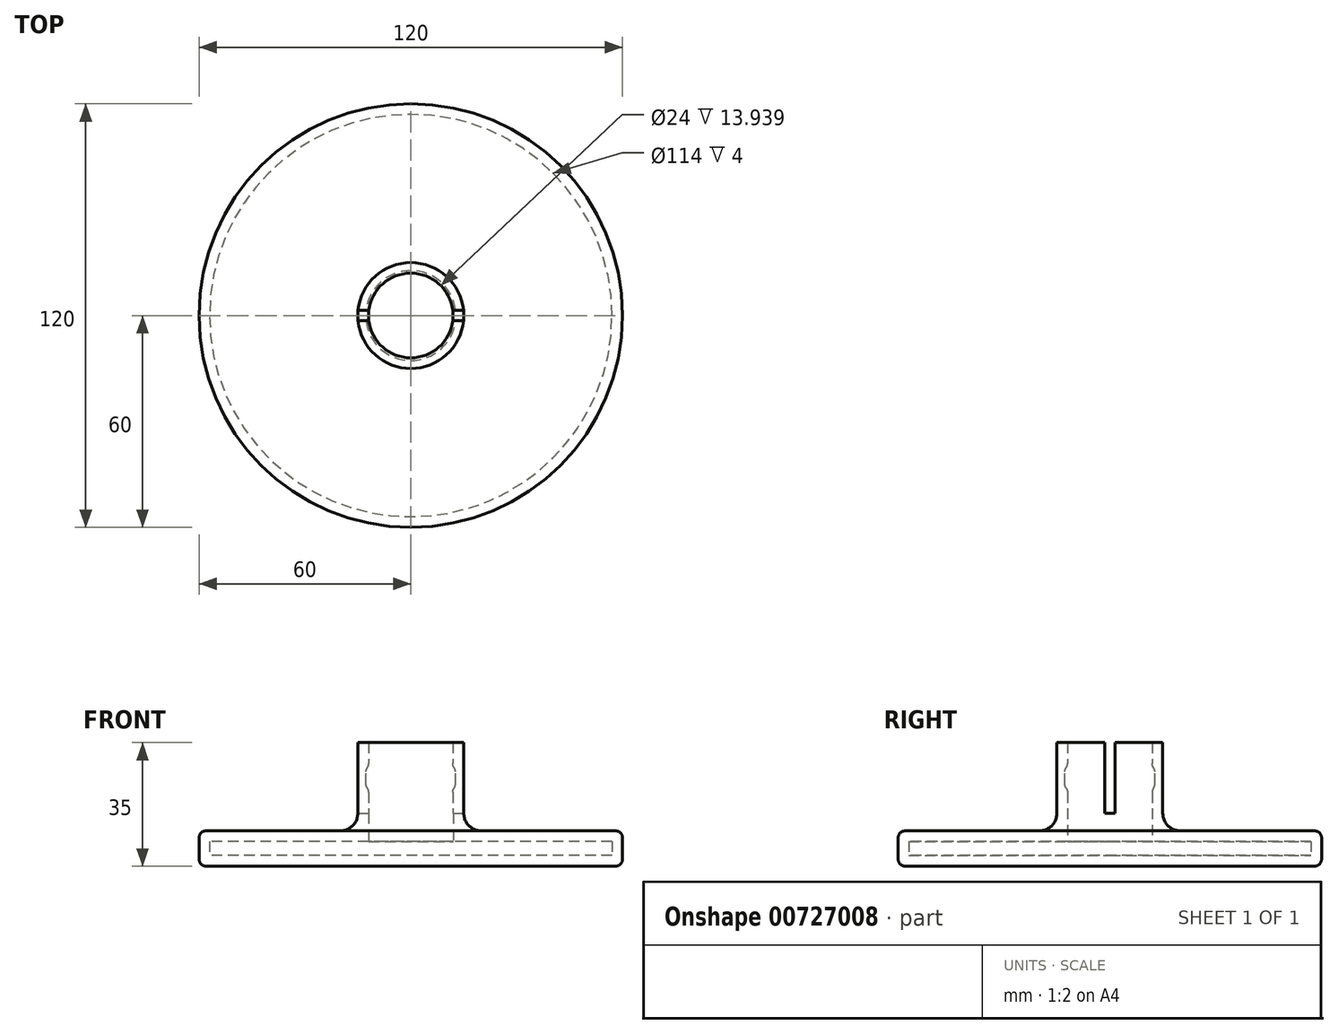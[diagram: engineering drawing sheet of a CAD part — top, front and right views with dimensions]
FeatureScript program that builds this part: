
annotation { "Feature Type Name" : "Feature", "Feature Type Description" : "" }
export const myFeature = defineFeature(function(context is Context, id is Id, definition is map)
    precondition{}
    {
        {
            var Q0;
            Q0=qCreatedBy(makeId("Top.planeOp"),FACE);
            var sketch = newSketch(context, id + "F0", { "sketchPlane" : qUnion([Q0])});
            skCircle(sketch, "E0", {"center": v(0, 0) * mm, "radius": 60 * mm});
            skCircle(sketch, "E1", {"center": v(0, 0) * mm, "radius": 15 * mm});
            skSolve(sketch);
        }
        {
            var Q0;
            Q0 = qSketchRegion(id + "F0", true);
            var Q1;
            Q1=makeQuery(id+"F0.imprint","IMPRINT",FACE,{"disambiguationData":[TD([[makeQuery(id+"F0.imprint","IMPRINT",EDGE,{"derivedFrom":sQuery(id+"F0.wireOp",EDGE,"E1")}),1.0]])]});
            extrude(context, id + "F1", {"entities" : qUnion([Q0, Q1]), "depth" : 10 * mm, "offsetDistance" : 25 * mm});
        }
        {
            var Q0;
            Q0=makeQuery(id+"F0.imprint","IMPRINT",FACE,{"disambiguationData":[TD([[makeQuery(id+"F0.imprint","IMPRINT",EDGE,{"derivedFrom":sQuery(id+"F0.wireOp",EDGE,"E1")}),1.0]])]});
            extrude(context, id + "F2", {"entities" : qUnion([Q0]), "operationType" : NewBodyOperationType.ADD, "depth" : 35 * mm, "offsetDistance" : 25 * mm});
        }
        {
            var Q0;
            Q0=makeQuery(id+"F2.opExtrude","CAP_FACE",FACE,{"disambiguationData":[OSD([sQuery(id+"F0.wireOp",EDGE,"E1")])],"isStart":false});
            shell(context, id + "F3", {"entities" : qUnion([Q0]), "thickness" : 3 * mm});
        }
        {
            var Q0;
            Q0=qCreatedBy(makeId("Right.planeOp"),FACE);
            var sketch = newSketch(context, id + "F4", { "sketchPlane" : qUnion([Q0])});
            skLineSegment(sketch, "E2.bottom", {"start": v(-1.5, 15) * mm, "end": v(1.5, 15) * mm});
            skLineSegment(sketch, "E2.top", {"start": v(-1.5, 35) * mm, "end": v(1.5, 35) * mm});
            skLineSegment(sketch, "E2.left", {"start": v(-1.5, 15) * mm, "end": v(-1.5, 35) * mm});
            skLineSegment(sketch, "E2.right", {"start": v(1.5, 15) * mm, "end": v(1.5, 35) * mm});
            skSolve(sketch);
        }
        {
            var Q0;
            Q0=makeQuery(id+"F4.imprint","IMPRINT",FACE,{"disambiguationData":[TD([[makeQuery(id+"F4.imprint","IMPRINT",EDGE,{"derivedFrom":sQuery(id+"F4.wireOp",EDGE,"E2.bottom")}),1.0]])]});
            extrude(context, id + "F5", {"entities" : qUnion([Q0]), "operationType" : NewBodyOperationType.REMOVE, "endBound" : BoundingType.SYMMETRIC, "oppositeDirection" : true, "depth" : 50 * mm, "offsetDistance" : 25 * mm});
        }
        {
            var Q0;
            Q0=qCreatedBy(makeId("Top.planeOp"),FACE);
            cPlane(context, id + "F6", {"entities" : qUnion([Q0]), "cplaneType" : CPlaneType.OFFSET, "offset" : 25 * mm, "width" : 150 * mm, "height" : 150 * mm});
        }
        {
            var Q0;
            Q0=qCreatedBy(id+"F6.planeOp",FACE);
            var sketch = newSketch(context, id + "F7", { "sketchPlane" : qUnion([Q0])});
            skCircle(sketch, "E3", {"center": v(0, 0) * mm, "radius": 12.75 * mm});
            skSolve(sketch);
        }
        {
            var Q0;
            Q0=makeQuery(id+"F7.imprint","IMPRINT",FACE,{"disambiguationData":[TD([[makeQuery(id+"F7.imprint","IMPRINT",EDGE,{"derivedFrom":sQuery(id+"F7.wireOp",EDGE,"E3")}),1.0]])]});
            extrude(context, id + "F8", {"entities" : qUnion([Q0]), "operationType" : NewBodyOperationType.REMOVE, "endBound" : BoundingType.SYMMETRIC, "oppositeDirection" : true, "depth" : 5 * mm, "offsetDistance" : 25 * mm});
        }
        {
            var Q0;
            Q0=makeQuery(id+"F2.boolean.opBoolean","INTERSECT",EDGE,{"derivedFrom":[makeQuery(id+"F1.opExtrude","CAP_FACE",FACE,{"disambiguationData":[OSD([sQuery(id+"F0.wireOp",EDGE,"E0")])],"isStart":false}),makeQuery(id+"F2.opExtrude","SWEPT_FACE",FACE,{"disambiguationData":[OSD([sQuery(id+"F0.wireOp",EDGE,"E1")])]})]});
            fillet(context, id + "F9", {"entities" : qUnion([Q0]), "radius" : 5 * mm, "tangentPropagation" : true, "allowEdgeOverflow" : false});
        }
        {
            var Q0;
            Q0=makeQuery(id+"F1.opExtrude","CAP_EDGE",EDGE,{"disambiguationData":[OSD([sQuery(id+"F0.wireOp",EDGE,"E0")])],"isStart":false});
            var Q1;
            Q1=makeQuery(id+"F1.opExtrude","CAP_EDGE",EDGE,{"disambiguationData":[OSD([sQuery(id+"F0.wireOp",EDGE,"E0")])],"isStart":true});
            fillet(context, id + "F10", {"entities" : qUnion([Q0, Q1]), "radius" : 2 * mm, "tangentPropagation" : true, "allowEdgeOverflow" : false});
        }
        {
            var Q0;
            Q0=makeQuery(id+"F8.boolean.opBoolean","INTERSECT",EDGE,{"disambiguationData":[OD(1.0)],"derivedFrom":[makeQuery(id+"F3.opShell","OFFSET_FACE",FACE,{"disambiguationData":[OSD([sQuery(id+"F0.wireOp",EDGE,"E1")])]}),makeQuery(id+"F8.opExtrude","CAP_FACE",FACE,{"disambiguationData":[OSD([sQuery(id+"F7.wireOp",EDGE,"E3")])],"isStart":false})]});
            var Q1;
            Q1=makeQuery(id+"F8.boolean.opBoolean","INTERSECT",EDGE,{"disambiguationData":[OD(1.0)],"derivedFrom":[makeQuery(id+"F3.opShell","OFFSET_FACE",FACE,{"disambiguationData":[OSD([sQuery(id+"F0.wireOp",EDGE,"E1")])]}),makeQuery(id+"F8.opExtrude","CAP_FACE",FACE,{"disambiguationData":[OSD([sQuery(id+"F7.wireOp",EDGE,"E3")])],"isStart":true})]});
            var Q2;
            Q2=makeQuery(id+"F8.boolean.opBoolean","INTERSECT",EDGE,{"disambiguationData":[OD(0.0)],"derivedFrom":[makeQuery(id+"F3.opShell","OFFSET_FACE",FACE,{"disambiguationData":[OSD([sQuery(id+"F0.wireOp",EDGE,"E1")])]}),makeQuery(id+"F8.opExtrude","CAP_FACE",FACE,{"disambiguationData":[OSD([sQuery(id+"F7.wireOp",EDGE,"E3")])],"isStart":false})]});
            var Q3;
            Q3=makeQuery(id+"F8.boolean.opBoolean","INTERSECT",EDGE,{"disambiguationData":[OD(0.0)],"derivedFrom":[makeQuery(id+"F3.opShell","OFFSET_FACE",FACE,{"disambiguationData":[OSD([sQuery(id+"F0.wireOp",EDGE,"E1")])]}),makeQuery(id+"F8.opExtrude","CAP_FACE",FACE,{"disambiguationData":[OSD([sQuery(id+"F7.wireOp",EDGE,"E3")])],"isStart":true})]});
            fillet(context, id + "F11", {"entities" : qUnion([Q0, Q1, Q2, Q3]), "radius" : 2 * mm, "tangentPropagation" : true, "allowEdgeOverflow" : false});
        }
        {
            var Q0;
            {var subQ0=makeQuery(id+"F5.opExtrude","SWEPT_FACE",FACE,{"disambiguationData":[OSD([sQuery(id+"F4.wireOp",EDGE,"E2.right")])]});var subQ1=sQuery(id+"F7.wireOp",EDGE,"E3");var subQ2=makeQuery(id+"F8.opExtrude","CAP_FACE",FACE,{"disambiguationData":[OSD([subQ1])],"isStart":false});Q0=makeQuery(id+"F11.opFillet","BLEND_EDGE",EDGE,{"blendedFrom":[makeQuery(id+"F8.boolean.opBoolean","INTERSECT",EDGE,{"disambiguationData":[OD(1.0)],"derivedFrom":[makeQuery(id+"F3.opShell","OFFSET_FACE",FACE,{"disambiguationData":[OSD([sQuery(id+"F0.wireOp",EDGE,"E1")])]}),subQ2]}),makeQuery(id+"F8.boolean.opBoolean","COPY",FACE,{"disambiguationData":[TD([makeQuery(id+"F5.boolean.opBoolean","COPY",FACE,{"disambiguationData":[OD(0.0)],"derivedFrom":subQ0})])],"derivedFrom":makeQuery(id+"F8.opExtrude","SWEPT_FACE",FACE,{"disambiguationData":[OSD([subQ1])]})})],"blendedInto":[makeQuery(id+"F8.boolean.opBoolean","COPY",FACE,{"disambiguationData":[TD([makeQuery(id+"F5.boolean.opBoolean","COPY",FACE,{"disambiguationData":[OD(0.0)],"derivedFrom":subQ0})])],"derivedFrom":makeQuery(id+"F8.opExtrude","SWEPT_FACE",FACE,{"disambiguationData":[OSD([subQ1])]})})]});}
            var Q1;
            {var subQ0=makeQuery(id+"F5.opExtrude","SWEPT_FACE",FACE,{"disambiguationData":[OSD([sQuery(id+"F4.wireOp",EDGE,"E2.right")])]});var subQ1=sQuery(id+"F7.wireOp",EDGE,"E3");var subQ2=makeQuery(id+"F8.opExtrude","CAP_FACE",FACE,{"disambiguationData":[OSD([subQ1])],"isStart":true});Q1=makeQuery(id+"F11.opFillet","BLEND_EDGE",EDGE,{"blendedFrom":[makeQuery(id+"F8.boolean.opBoolean","INTERSECT",EDGE,{"disambiguationData":[OD(1.0)],"derivedFrom":[makeQuery(id+"F3.opShell","OFFSET_FACE",FACE,{"disambiguationData":[OSD([sQuery(id+"F0.wireOp",EDGE,"E1")])]}),subQ2]}),makeQuery(id+"F8.boolean.opBoolean","COPY",FACE,{"disambiguationData":[TD([makeQuery(id+"F5.boolean.opBoolean","COPY",FACE,{"disambiguationData":[OD(0.0)],"derivedFrom":subQ0})])],"derivedFrom":makeQuery(id+"F8.opExtrude","SWEPT_FACE",FACE,{"disambiguationData":[OSD([subQ1])]})})],"blendedInto":[makeQuery(id+"F8.boolean.opBoolean","COPY",FACE,{"disambiguationData":[TD([makeQuery(id+"F5.boolean.opBoolean","COPY",FACE,{"disambiguationData":[OD(0.0)],"derivedFrom":subQ0})])],"derivedFrom":makeQuery(id+"F8.opExtrude","SWEPT_FACE",FACE,{"disambiguationData":[OSD([subQ1])]})})]});}
            var Q2;
            {var subQ0=makeQuery(id+"F5.opExtrude","SWEPT_FACE",FACE,{"disambiguationData":[OSD([sQuery(id+"F4.wireOp",EDGE,"E2.left")])]});var subQ1=sQuery(id+"F7.wireOp",EDGE,"E3");var subQ2=makeQuery(id+"F8.opExtrude","CAP_FACE",FACE,{"disambiguationData":[OSD([subQ1])],"isStart":true});Q2=makeQuery(id+"F11.opFillet","BLEND_EDGE",EDGE,{"blendedFrom":[makeQuery(id+"F8.boolean.opBoolean","INTERSECT",EDGE,{"disambiguationData":[OD(0.0)],"derivedFrom":[makeQuery(id+"F3.opShell","OFFSET_FACE",FACE,{"disambiguationData":[OSD([sQuery(id+"F0.wireOp",EDGE,"E1")])]}),subQ2]}),makeQuery(id+"F8.boolean.opBoolean","COPY",FACE,{"disambiguationData":[TD([makeQuery(id+"F5.boolean.opBoolean","COPY",FACE,{"disambiguationData":[OD(0.0)],"derivedFrom":subQ0})])],"derivedFrom":makeQuery(id+"F8.opExtrude","SWEPT_FACE",FACE,{"disambiguationData":[OSD([subQ1])]})})],"blendedInto":[makeQuery(id+"F8.boolean.opBoolean","COPY",FACE,{"disambiguationData":[TD([makeQuery(id+"F5.boolean.opBoolean","COPY",FACE,{"disambiguationData":[OD(0.0)],"derivedFrom":subQ0})])],"derivedFrom":makeQuery(id+"F8.opExtrude","SWEPT_FACE",FACE,{"disambiguationData":[OSD([subQ1])]})})]});}
            var Q3;
            {var subQ0=makeQuery(id+"F5.opExtrude","SWEPT_FACE",FACE,{"disambiguationData":[OSD([sQuery(id+"F4.wireOp",EDGE,"E2.left")])]});var subQ1=sQuery(id+"F7.wireOp",EDGE,"E3");var subQ2=makeQuery(id+"F8.opExtrude","CAP_FACE",FACE,{"disambiguationData":[OSD([subQ1])],"isStart":false});Q3=makeQuery(id+"F11.opFillet","BLEND_EDGE",EDGE,{"blendedFrom":[makeQuery(id+"F8.boolean.opBoolean","INTERSECT",EDGE,{"disambiguationData":[OD(0.0)],"derivedFrom":[makeQuery(id+"F3.opShell","OFFSET_FACE",FACE,{"disambiguationData":[OSD([sQuery(id+"F0.wireOp",EDGE,"E1")])]}),subQ2]}),makeQuery(id+"F8.boolean.opBoolean","COPY",FACE,{"disambiguationData":[TD([makeQuery(id+"F5.boolean.opBoolean","COPY",FACE,{"disambiguationData":[OD(0.0)],"derivedFrom":subQ0})])],"derivedFrom":makeQuery(id+"F8.opExtrude","SWEPT_FACE",FACE,{"disambiguationData":[OSD([subQ1])]})})],"blendedInto":[makeQuery(id+"F8.boolean.opBoolean","COPY",FACE,{"disambiguationData":[TD([makeQuery(id+"F5.boolean.opBoolean","COPY",FACE,{"disambiguationData":[OD(0.0)],"derivedFrom":subQ0})])],"derivedFrom":makeQuery(id+"F8.opExtrude","SWEPT_FACE",FACE,{"disambiguationData":[OSD([subQ1])]})})]});}
            fillet(context, id + "F12", {"entities" : qUnion([Q0, Q1, Q2, Q3]), "radius" : 2 * mm, "tangentPropagation" : true, "allowEdgeOverflow" : false});
        }
    });
